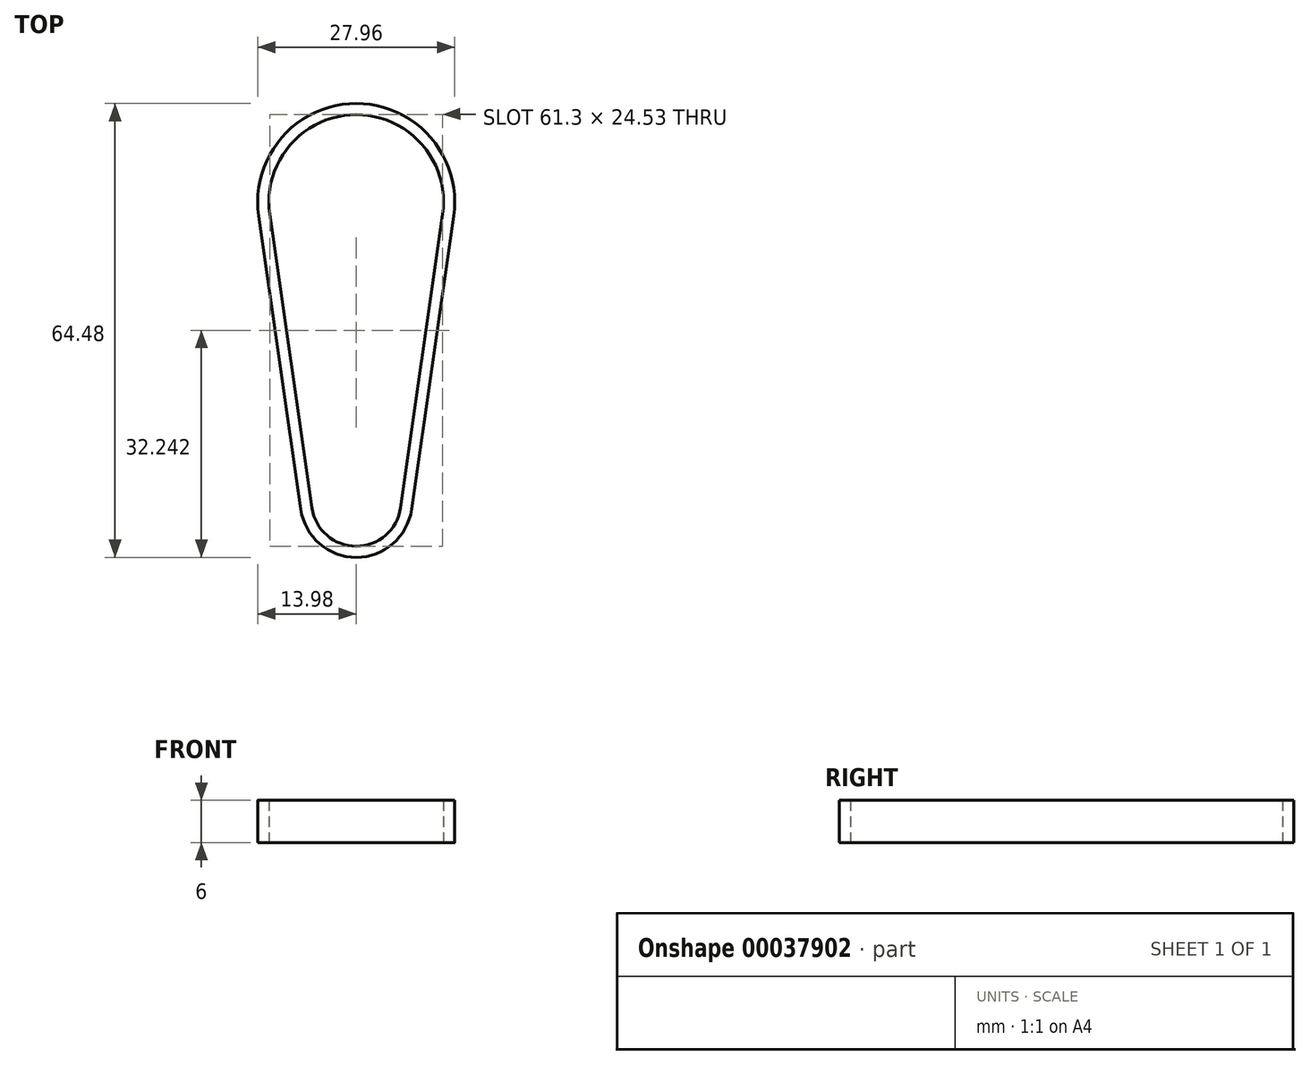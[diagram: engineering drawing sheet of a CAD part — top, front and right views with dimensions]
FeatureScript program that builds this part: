
annotation { "Feature Type Name" : "Feature", "Feature Type Description" : "" }
export const myFeature = defineFeature(function(context is Context, id is Id, definition is map)
    precondition{}
    {
        {
            var Q0;
            Q0=qCreatedBy(makeId("Top.planeOp"),FACE);
            var sketch = newSketch(context, id + "F0", { "sketchPlane" : qUnion([Q0])});
            skLineSegment(sketch, "E0", {"start": v(0, 0) * mm, "end": v(0, -42.56) * mm});
            skCircle(sketch, "E1", {"center": v(0, 0) * mm, "radius": 12.4 * mm, "construction": true});
            skCircle(sketch, "E2", {"center": v(0, -42.56) * mm, "radius": 6.35 * mm, "construction": true});
            skLineSegment(sketch, "E3", {"start": v(-12.27, -1.76) * mm, "end": v(-6.29, -43.46) * mm});
            skLineSegment(sketch, "E4", {"start": v(12.27, -1.76) * mm, "end": v(6.29, -43.46) * mm});
            skLineSegment(sketch, "E5", {"start": v(-9.28, -22.61) * mm, "end": v(-10.85, -22.84) * mm, "construction": true});
            skLineSegment(sketch, "E6", {"start": v(9.28, -22.61) * mm, "end": v(10.85, -22.84) * mm, "construction": true});
            skArc(sketch, "E7", {"start": v(-6.29, -43.46) * mm, "mid": v(0, -48.9) * mm, "end": v(6.29, -43.46) * mm});
            skArc(sketch, "E8", {"start": v(12.27, -1.76) * mm, "mid": v(0, 12.4) * mm, "end": v(-12.27, -1.76) * mm});
            skLineSegment(sketch, "E9", {"start": v(-13.84, -1.98) * mm, "end": v(-7.86, -43.69) * mm});
            skLineSegment(sketch, "E10", {"start": v(13.84, -1.98) * mm, "end": v(7.86, -43.69) * mm});
            skArc(sketch, "E11", {"start": v(13.84, -1.98) * mm, "mid": v(0, 13.98) * mm, "end": v(-13.84, -1.98) * mm});
            skArc(sketch, "E12", {"start": v(-7.86, -43.69) * mm, "mid": v(0, -50.5) * mm, "end": v(7.86, -43.69) * mm});
            skSolve(sketch);
        }
        {
            var Q0;
            Q0 = qSketchRegion(id + "F0", true);
            extrude(context, id + "F1", {"entities" : qUnion([Q0]), "depth" : 6 * mm});
        }
    });
